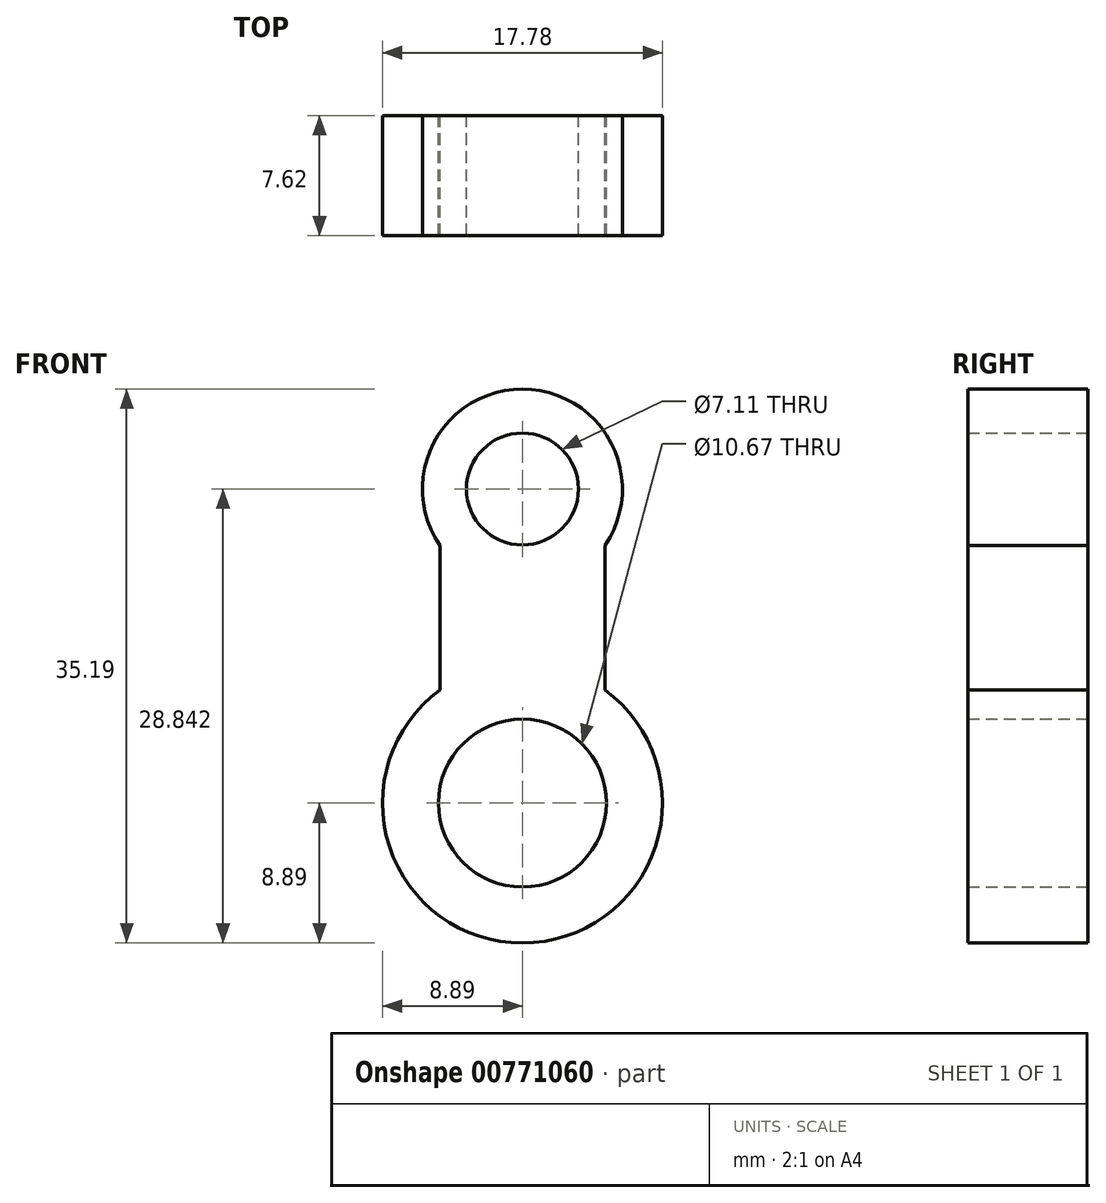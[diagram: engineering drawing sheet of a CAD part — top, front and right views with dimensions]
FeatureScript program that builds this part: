
annotation { "Feature Type Name" : "Feature", "Feature Type Description" : "" }
export const myFeature = defineFeature(function(context is Context, id is Id, definition is map)
    precondition{}
    {
        {
            var Q0;
            Q0=qCreatedBy(makeId("Front.planeOp"),FACE);
            var sketch = newSketch(context, id + "F0", { "sketchPlane" : qUnion([Q0])});
            skCircle(sketch, "E0", {"center": v(0, 0) * mm, "radius": 8.9 * mm});
            skCircle(sketch, "E1", {"center": v(0, 0) * mm, "radius": 5.33 * mm});
            skCircle(sketch, "E2", {"center": v(0, 19.95) * mm, "radius": 3.56 * mm});
            skCircle(sketch, "E3", {"center": v(0, 19.95) * mm, "radius": 6.35 * mm});
            skLineSegment(sketch, "E4", {"start": v(0, 19.95) * mm, "end": v(-6.35, 19.95) * mm, "construction": true});
            skLineSegment(sketch, "E5", {"start": v(0, 19.95) * mm, "end": v(6.35, 19.95) * mm, "construction": true});
            skLineSegment(sketch, "E6", {"start": v(3.56, 19.95) * mm, "end": v(5.23, 16.35) * mm, "construction": true});
            skLineSegment(sketch, "E7", {"start": v(5.23, 16.35) * mm, "end": v(5.23, 7.19) * mm});
            skLineSegment(sketch, "E8", {"start": v(-3.56, 19.95) * mm, "end": v(-5.23, 16.35) * mm, "construction": true});
            skLineSegment(sketch, "E9", {"start": v(-5.23, 16.35) * mm, "end": v(-5.23, 7.19) * mm});
            skSolve(sketch);
        }
        {
            var Q0;
            {var subQ0=sQuery(id+"F0.wireOp",EDGE,"E7");Q0=makeQuery(id+"F0.imprint","IMPRINT",FACE,{"disambiguationData":[TD([[makeQuery(id+"F0.imprint","IMPRINT",EDGE,{"derivedFrom":subQ0}),-1.0]])]});}
            var Q1;
            Q1=makeQuery(id+"F0.imprint","IMPRINT",FACE,{"disambiguationData":[TD([[makeQuery(id+"F0.imprint","IMPRINT",EDGE,{"derivedFrom":sQuery(id+"F0.wireOp",EDGE,"E2")}),-1.0]])]});
            var Q2;
            Q2=makeQuery(id+"F0.imprint","IMPRINT",FACE,{"disambiguationData":[TD([[makeQuery(id+"F0.imprint","IMPRINT",EDGE,{"derivedFrom":sQuery(id+"F0.wireOp",EDGE,"E1")}),-1.0]])]});
            extrude(context, id + "F1", {"entities" : qUnion([Q0, Q1, Q2]), "depth" : 7.62 * mm, "offsetDistance" : 25.4 * mm});
        }
    });
